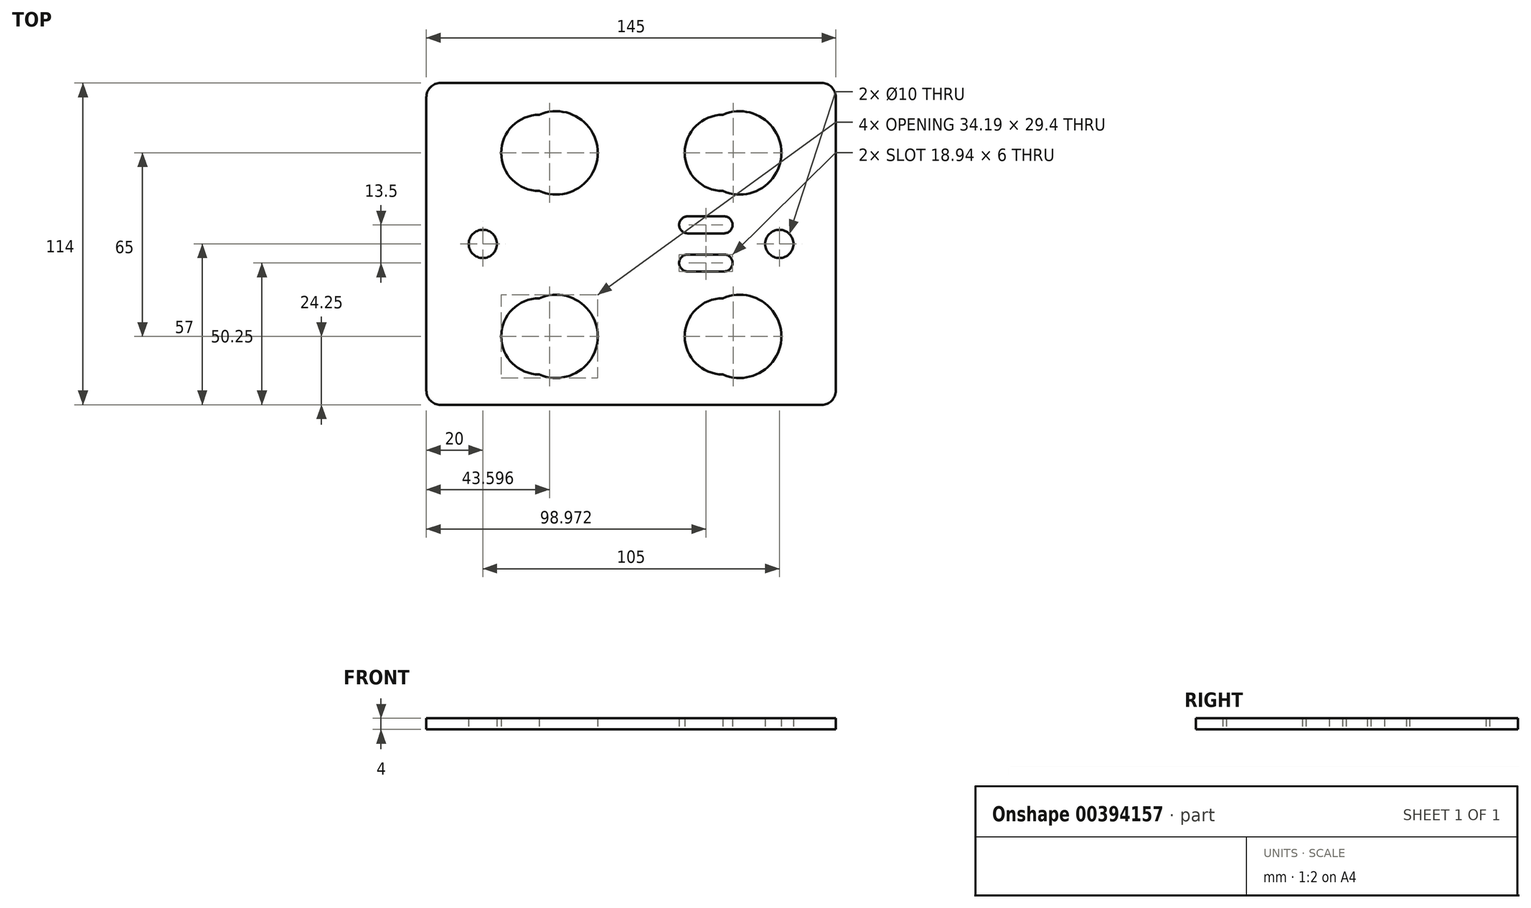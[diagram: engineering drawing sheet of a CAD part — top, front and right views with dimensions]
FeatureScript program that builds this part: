
annotation { "Feature Type Name" : "Feature", "Feature Type Description" : "" }
export const myFeature = defineFeature(function(context is Context, id is Id, definition is map)
    precondition{}
    {
        {
            var Q0;
            Q0=qCreatedBy(makeId("Top.planeOp"),FACE);
            var sketch = newSketch(context, id + "F0", { "sketchPlane" : qUnion([Q0])});
            skLineSegment(sketch, "E0.bottom", {"start": v(-67.5, 57) * mm, "end": v(67.5, 57) * mm});
            skLineSegment(sketch, "E0.top", {"start": v(-67.5, -57) * mm, "end": v(67.5, -57) * mm});
            skLineSegment(sketch, "E0.right", {"start": v(72.5, 52) * mm, "end": v(72.5, -52) * mm});
            skArc(sketch, "E1", {"start": v(-32.5, 45.75) * mm, "mid": v(-46, 32.25) * mm, "end": v(-32.5, 18.75) * mm});
            skArc(sketch, "E2", {"start": v(-32.5, 18.75) * mm, "mid": v(-11.8, 32.25) * mm, "end": v(-32.5, 45.75) * mm});
            skArc(sketch, "E3.0.1.0", {"start": v(-32.5, -19.25) * mm, "mid": v(-46, -32.75) * mm, "end": v(-32.5, -46.25) * mm});
            skArc(sketch, "E3.0.1.1", {"start": v(-32.5, -46.25) * mm, "mid": v(-11.8, -32.75) * mm, "end": v(-32.5, -19.25) * mm});
            skArc(sketch, "E3.1.0.0", {"start": v(32.5, 45.75) * mm, "mid": v(19, 32.25) * mm, "end": v(32.5, 18.75) * mm});
            skArc(sketch, "E3.1.0.1", {"start": v(32.5, 18.75) * mm, "mid": v(53.2, 32.25) * mm, "end": v(32.5, 45.75) * mm});
            skArc(sketch, "E3.1.1.0", {"start": v(32.5, -19.25) * mm, "mid": v(19, -32.75) * mm, "end": v(32.5, -46.25) * mm});
            skArc(sketch, "E3.1.1.1", {"start": v(32.5, -46.25) * mm, "mid": v(53.2, -32.75) * mm, "end": v(32.5, -19.25) * mm});
            skLineSegment(sketch, "E3.direction1", {"start": v(-32.5, 18.75) * mm, "end": v(32.5, 18.75) * mm, "construction": true});
            skLineSegment(sketch, "E3.direction2", {"start": v(-32.5, 18.75) * mm, "end": v(-32.5, -46.25) * mm, "construction": true});
            skArc(sketch, "E4.filletArc", {"start": v(-67.5, 57) * mm, "mid": v(-71.04, 55.54) * mm, "end": v(-72.5, 52) * mm});
            skPoint(sketch, "E5.visualSharp", {"position": v(72.5, 57) * mm});
            skArc(sketch, "E5.filletArc", {"start": v(72.5, 52) * mm, "mid": v(71.04, 55.54) * mm, "end": v(67.5, 57) * mm});
            skPoint(sketch, "E6.visualSharp", {"position": v(72.5, -57) * mm});
            skArc(sketch, "E6.filletArc", {"start": v(67.5, -57) * mm, "mid": v(71.04, -55.54) * mm, "end": v(72.5, -52) * mm});
            skLineSegment(sketch, "E7", {"start": v(-72.5, -52) * mm, "end": v(-72.5, 52) * mm});
            skCircle(sketch, "E8", {"center": v(-52.5, 0) * mm, "radius": 5 * mm});
            skCircle(sketch, "E9", {"center": v(52.5, 0) * mm, "radius": 5 * mm});
            skArc(sketch, "E10", {"start": v(20, 9.75) * mm, "mid": v(17, 6.75) * mm, "end": v(20, 3.75) * mm});
            skArc(sketch, "E11", {"start": v(32.94, 3.75) * mm, "mid": v(35.94, 6.75) * mm, "end": v(32.94, 9.75) * mm});
            skLineSegment(sketch, "E12", {"start": v(20, 9.75) * mm, "end": v(32.94, 9.75) * mm});
            skLineSegment(sketch, "E13", {"start": v(20, 3.75) * mm, "end": v(32.94, 3.75) * mm});
            skLineSegment(sketch, "E14.1.0.0", {"start": v(20, -3.75) * mm, "end": v(32.94, -3.75) * mm});
            skLineSegment(sketch, "E14.1.0.1", {"start": v(20, -9.75) * mm, "end": v(32.94, -9.75) * mm});
            skArc(sketch, "E14.1.0.2", {"start": v(32.94, -9.75) * mm, "mid": v(35.94, -6.75) * mm, "end": v(32.94, -3.75) * mm});
            skArc(sketch, "E14.1.0.3", {"start": v(20, -3.75) * mm, "mid": v(17, -6.75) * mm, "end": v(20, -9.75) * mm});
            skLineSegment(sketch, "E14.direction1", {"start": v(20, 3.75) * mm, "end": v(20, -9.75) * mm, "construction": true});
            skLineSegment(sketch, "E15", {"start": v(-72.5, 0) * mm, "end": v(72.5, 0) * mm, "construction": true});
            skPoint(sketch, "E16.orphan", {"position": v(-72.5, -52) * mm});
            skPoint(sketch, "E17.visualSharp", {"position": v(-72.5, -57) * mm});
            skArc(sketch, "E17.filletArc", {"start": v(-72.5, -52) * mm, "mid": v(-71.04, -55.54) * mm, "end": v(-67.5, -57) * mm});
            skLineSegment(sketch, "E18", {"start": v(-32.5, 18.75) * mm, "end": v(-32.5, 32.25) * mm});
            skLineSegment(sketch, "E19", {"start": v(-32.5, 45.75) * mm, "end": v(-32.5, 32.25) * mm});
            skSolve(sketch);
        }
        {
            var Q0;
            Q0=makeQuery(id+"F0.imprint","IMPRINT",FACE,{"disambiguationData":[TD([[makeQuery(id+"F0.imprint","IMPRINT",EDGE,{"derivedFrom":sQuery(id+"F0.wireOp",EDGE,"E0.bottom")}),-1.0]])]});
            extrude(context, id + "F1", {"entities" : qUnion([Q0]), "depth" : 4 * mm});
        }
    });
